# Revit family: Gira_016130
name_source: partatom
category: Electrical Fixtures
revit_build: Autodesk Revit 2017 (Build: 20160225_1515(x64)
units: mm (PartAtom-declared; Revit-internal decimal feet)

## family parameters
Cut with Voids When Loaded = No
Host = Face
Maintain Annotation Orientation = No
Part Type = Normal
Room Calculation Point = No
Round Connector Dimension = Use Diameter
Shared = No

## types (1)
- Light sig. bayonet WP SM grey
    Application as button = no
    Assembly arrangement = Complete device
    BIM = https://media.live.bim.site
    BIMSITE_PRODUCT_ID = 57a1897e5d60618b5328bcd689d0aa10b587ea38
    Colour = Grey
    Cost = 0 $
    Default Elevation = 1219 mm
    Description = Light sig.bayon. WP SM GY Light signal with bayonet lock,grey Notes : - The following devices are delivered without mounting plate. - Not suitable for continuous operation.
    GTIN = 4010337161301
    HAN = 016130
    Halogen free = No
    HeinzeBIM = https://www.heinze.de
    Lamp holder = Sonstige (*de-DE)
    Manufacturer = Gira
    Material = plastic
    Material quality = Thermoplastic
    Suitable for degree of protection (IP) = IP44
    Surface protection = Sonstige (*de-DE)
    Transparent = No
    Type of fastening = Screw mounting
    URL = https://www.gira.de
    With flashlight = No
    With light source = No

## geometry (parser evidence)
native form markers: Blend x2, Sweep x9
no freeform markers — native parametric forms only
